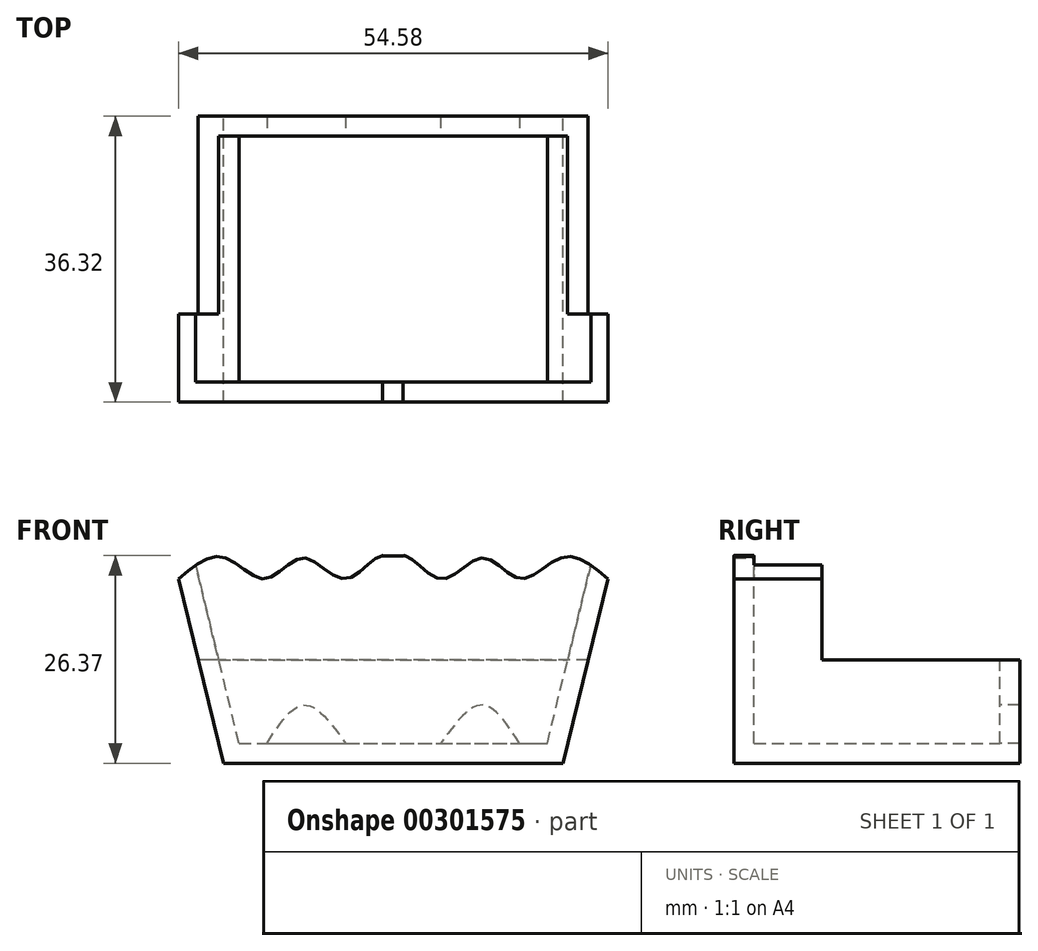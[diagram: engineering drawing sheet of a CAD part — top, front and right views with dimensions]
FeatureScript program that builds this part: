
annotation { "Feature Type Name" : "Feature", "Feature Type Description" : "" }
export const myFeature = defineFeature(function(context is Context, id is Id, definition is map)
    precondition{}
    {
        {
            var Q0;
            Q0=qCreatedBy(makeId("Front.planeOp"),FACE);
            var sketch = newSketch(context, id + "F0", { "sketchPlane" : qUnion([Q0])});
            skLineSegment(sketch, "E0", {"start": v(-36.3, 23.43) * mm, "end": v(6.86, 23.43) * mm});
            skPoint(sketch, "E1.start.orphan", {"position": v(-14.72, 23.43) * mm});
            skLineSegment(sketch, "E2", {"start": v(-36.3, 23.43) * mm, "end": v(-42, 46.86) * mm});
            skLineSegment(sketch, "E3", {"start": v(-14.72, 73.15) * mm, "end": v(-14.72, -64) * mm, "construction": true});
            skLineSegment(sketch, "E4.MirrorCS", {"start": v(6.86, 23.43) * mm, "end": v(12.57, 46.86) * mm});
            skFitSpline(sketch, "E5", {"points": [v(-42, 46.86) * mm, v(-36.3, 49.62) * mm, v(-30.97, 46.86) * mm, v(-26.1, 49.5) * mm, v(-20.88, 46.86) * mm, v(-16.46, 49.74) * mm, v(-14.72, 48.94) * mm], "startDerivative": vector(30.6, 25.86) * mm, "endDerivative": vector(15.24, -14.98) * mm});
            skFitSpline(sketch, "E6.MirrorCS", {"points": [v(12.57, 46.86) * mm, v(6.87, 49.62) * mm, v(1.54, 46.86) * mm, v(-3.34, 49.5) * mm, v(-8.55, 46.86) * mm, v(-12.98, 49.74) * mm, v(-14.72, 48.94) * mm], "startDerivative": vector(-30.6, 25.86) * mm, "endDerivative": vector(-15.24, -14.98) * mm});
            skFitSpline(sketch, "E7", {"points": [v(-16.16, 49.8) * mm, v(-14.77, 49.79) * mm, v(-13.13, 49.78) * mm], "startDerivative": vector(3.03, -0.02) * mm, "endDerivative": vector(3.03, -0.02) * mm});
            skLineSegment(sketch, "E8", {"start": v(-52.56, -56.58) * mm, "end": v(-53.72, -56.58) * mm});
            skLineSegment(sketch, "E9", {"start": v(23.13, -56.58) * mm, "end": v(24.29, -56.58) * mm});
            skPoint(sketch, "E10.orphan", {"position": v(-35.28, 22.73) * mm});
            skPoint(sketch, "E11.MirrorCS.start.orphan", {"position": v(5.85, 22.73) * mm});
            skSolve(sketch);
        }
        {
            var Q0;
            Q0 = qSketchRegion(id + "F0", true);
            extrude(context, id + "F1", {"entities" : qUnion([Q0]), "depth" : 36.32 * mm});
        }
        {
            var Q0;
            Q0=makeQuery(id+"F1.opExtrude","SWEPT_FACE",FACE,{"disambiguationData":[OSD([sQuery(id+"F0.wireOp",EDGE,"E5")])]});
            var Q1;
            Q1=makeQuery(id+"F1.opExtrude","SWEPT_FACE",FACE,{"disambiguationData":[OSD([sQuery(id+"F0.wireOp",EDGE,"E6.MirrorCS")])]});
            var Q2;
            Q2=makeQuery(id+"F1.opExtrude","SWEPT_FACE",FACE,{"disambiguationData":[OSD([sQuery(id+"F0.wireOp",EDGE,"E7")])]});
            shell(context, id + "F2", {"entities" : qUnion([Q0, Q1, Q2]), "thickness" : 2.54 * mm});
        }
        {
            var Q0;
            Q0=makeQuery(id+"F1.opExtrude","CAP_FACE",FACE,{"disambiguationData":[OSD([sQuery(id+"F0.wireOp",EDGE,"E2"),sQuery(id+"F0.wireOp",EDGE,"E4.MirrorCS"),sQuery(id+"F0.wireOp",EDGE,"E5"),sQuery(id+"F0.wireOp",EDGE,"E6.MirrorCS"),sQuery(id+"F0.wireOp",EDGE,"E7"),sQuery(id+"F0.wireOp",EDGE,"E0")])],"isStart":true});
            var sketch = newSketch(context, id + "F3", { "sketchPlane" : qUnion([Q0])});
            skLineSegment(sketch, "E12", {"start": v(-10.06, 36.55) * mm, "end": v(39.5, 36.55) * mm});
            skSolve(sketch);
        }
        {
            var Q0;
            Q0 = qSketchRegion(id + "F3", true);
            var Q1;
            {var subQ2=sQuery(id+"F3.wireOp",EDGE,"E12");Q1=makeQuery(id+"F3.imprint","IMPRINT",FACE,{"disambiguationData":[TD([[makeQuery(id+"F3.imprint","IMPRINT",EDGE,{"derivedFrom":subQ2}),1.0]])]});}
            extrude(context, id + "F4", {"entities" : qUnion([Q0, Q1]), "operationType" : NewBodyOperationType.REMOVE, "oppositeDirection" : true, "depth" : 25.15 * mm});
        }
        {
            var Q0;
            {var subQ0=sQuery(id+"F0.wireOp",EDGE,"E0");var subQ1=sQuery(id+"F0.wireOp",EDGE,"E7");var subQ2=sQuery(id+"F0.wireOp",EDGE,"E6.MirrorCS");var subQ3=sQuery(id+"F0.wireOp",EDGE,"E5");var subQ4=sQuery(id+"F0.wireOp",EDGE,"E4.MirrorCS");var subQ5=sQuery(id+"F0.wireOp",EDGE,"E2");Q0=makeQuery(id+"F2.opShell","OFFSET_FACE",FACE,{"disambiguationData":[OSD([subQ5,subQ4,subQ3,subQ2,subQ1,subQ0]),TDD([makeQuery(id+"F1.opExtrude","CAP_FACE",FACE,{"disambiguationData":[OSD([subQ5,subQ4,subQ3,subQ2,subQ1,subQ0])],"isStart":true})])]});}
            var sketch = newSketch(context, id + "F5", { "sketchPlane" : qUnion([Q0])});
            skLineSegment(sketch, "E13", {"start": v(-14.72, 60.7) * mm, "end": v(-14.72, 0) * mm, "construction": true});
            skPoint(sketch, "E13.startSnap0", {"position": v(-14.72, 36.55) * mm});
            skPoint(sketch, "E13.endSnap0", {"position": v(-14.72, 23.43) * mm});
            skPoint(sketch, "E14.MirrorCS.end.orphan", {"position": v(-2.47, 23.43) * mm});
            skPoint(sketch, "E14.MirrorCS.start.orphan", {"position": v(11, 23.43) * mm});
            skPoint(sketch, "E15.end.orphan", {"position": v(-26.96, 23.43) * mm});
            skPoint(sketch, "E15.start.orphan", {"position": v(-40.43, 23.43) * mm});
            skFitSpline(sketch, "E16", {"points": [v(-30.77, 25.97) * mm, v(-26, 30.82) * mm, v(-20.75, 25.97) * mm], "startDerivative": vector(9.48, 14.62) * mm, "endDerivative": vector(10.54, -14.5) * mm});
            skFitSpline(sketch, "E17.MirrorCS", {"points": [v(1.33, 25.97) * mm, v(-3.43, 30.82) * mm, v(-8.68, 25.97) * mm], "startDerivative": vector(-9.48, 14.62) * mm, "endDerivative": vector(-10.54, -14.5) * mm});
            skSolve(sketch);
        }
        {
            var Q0;
            {var subQ0=sQuery(id+"F5.wireOp",EDGE,"E16");Q0=makeQuery(id+"F5.imprint","IMPRINT",FACE,{"disambiguationData":[TD([[makeQuery(id+"F5.imprint","IMPRINT",EDGE,{"derivedFrom":subQ0}),-1.0]])]});}
            var Q1;
            {var subQ0=sQuery(id+"F5.wireOp",EDGE,"E17.MirrorCS");Q1=makeQuery(id+"F5.imprint","IMPRINT",FACE,{"disambiguationData":[TD([[makeQuery(id+"F5.imprint","IMPRINT",EDGE,{"derivedFrom":subQ0}),1.0]])]});}
            extrude(context, id + "F6", {"entities" : qUnion([Q0, Q1]), "operationType" : NewBodyOperationType.REMOVE, "oppositeDirection" : true, "depth" : 32.77 * mm});
        }
    });
